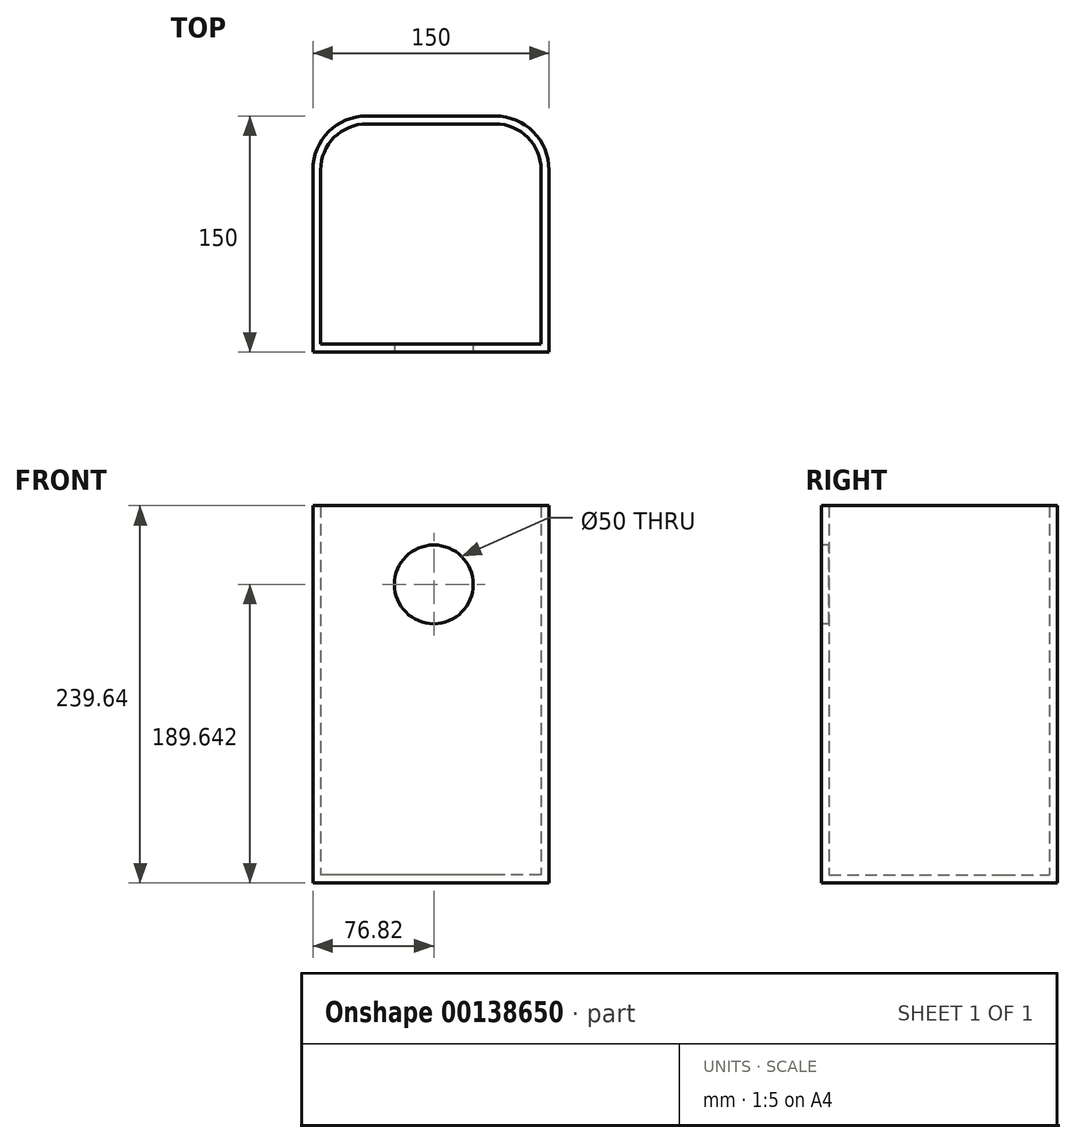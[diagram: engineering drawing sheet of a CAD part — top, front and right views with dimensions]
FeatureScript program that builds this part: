
annotation { "Feature Type Name" : "Feature", "Feature Type Description" : "" }
export const myFeature = defineFeature(function(context is Context, id is Id, definition is map)
    precondition{}
    {
        {
            var Q0;
            Q0=qCreatedBy(makeId("Top.planeOp"),FACE);
            var sketch = newSketch(context, id + "F0", { "sketchPlane" : qUnion([Q0])});
            skLineSegment(sketch, "E0.bottom", {"start": v(73.18, -69) * mm, "end": v(-76.82, -69) * mm});
            skLineSegment(sketch, "E0.top", {"start": v(73.18, 81) * mm, "end": v(-76.82, 81) * mm});
            skLineSegment(sketch, "E0.left", {"start": v(73.18, -69) * mm, "end": v(73.18, 81) * mm});
            skLineSegment(sketch, "E0.right", {"start": v(-76.82, -69) * mm, "end": v(-76.82, 81) * mm});
            skLineSegment(sketch, "E1", {"start": v(-1.82, 81) * mm, "end": v(0, 0) * mm});
            skSolve(sketch);
        }
        {
            var Q0;
            Q0=makeQuery(id+"F0.imprint","IMPRINT",FACE,{"disambiguationData":[TD([[makeQuery(id+"F0.imprint","IMPRINT",EDGE,{"derivedFrom":sQuery(id+"F0.wireOp",EDGE,"E0.bottom")}),-1.0]])]});
            extrude(context, id + "F1", {"entities" : qUnion([Q0]), "endBound" : BoundingType.SYMMETRIC, "depth" : 239.65 * mm, "offsetDistance" : 25 * mm});
        }
        {
            var Q0;
            Q0=makeQuery(id+"F1.opExtrude","SWEPT_EDGE",EDGE,{"disambiguationData":[OSD([sQuery(id+"F0.wireOp",EDGE,"E0.top"),sQuery(id+"F0.wireOp",EDGE,"E0.left")])]});
            var Q1;
            Q1=makeQuery(id+"F1.opExtrude","SWEPT_EDGE",EDGE,{"disambiguationData":[OSD([sQuery(id+"F0.wireOp",EDGE,"E0.top"),sQuery(id+"F0.wireOp",EDGE,"E0.right")])]});
            fillet(context, id + "F2", {"entities" : qUnion([Q0, Q1]), "radius" : 34.25 * mm, "tangentPropagation" : true, "allowEdgeOverflow" : false});
        }
        {
            var Q0;
            Q0=makeQuery(id+"F1.opExtrude","CAP_FACE",FACE,{"disambiguationData":[OSD([sQuery(id+"F0.wireOp",EDGE,"E0.bottom"),sQuery(id+"F0.wireOp",EDGE,"E0.top"),sQuery(id+"F0.wireOp",EDGE,"E0.left"),sQuery(id+"F0.wireOp",EDGE,"E0.right")])],"isStart":false});
            shell(context, id + "F3", {"entities" : qUnion([Q0]), "thickness" : 5 * mm});
        }
        {
            var Q0;
            Q0=makeQuery(id+"F1.opExtrude","SWEPT_FACE",FACE,{"disambiguationData":[OSD([sQuery(id+"F0.wireOp",EDGE,"E0.bottom")])]});
            var sketch = newSketch(context, id + "F4", { "sketchPlane" : qUnion([Q0])});
            skCircle(sketch, "E2", {"center": v(0, 69.82) * mm, "radius": 25 * mm});
            skSolve(sketch);
        }
        {
            var Q0;
            Q0=makeQuery(id+"F4.imprint","IMPRINT",FACE,{"disambiguationData":[TD([[makeQuery(id+"F4.imprint","IMPRINT",EDGE,{"derivedFrom":sQuery(id+"F4.wireOp",EDGE,"E2")}),1.0]])]});
            extrude(context, id + "F5", {"entities" : qUnion([Q0]), "operationType" : NewBodyOperationType.REMOVE, "oppositeDirection" : true, "depth" : 25 * mm, "offsetDistance" : 25 * mm});
        }
    });
